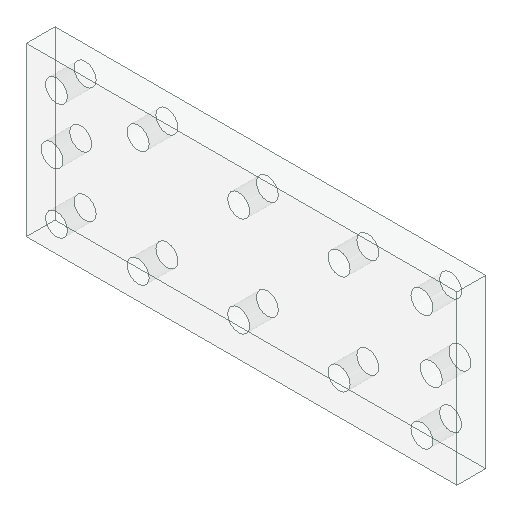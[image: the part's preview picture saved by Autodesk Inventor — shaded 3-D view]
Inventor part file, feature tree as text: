
AUTODESK INVENTOR PART (.ipt)
format: ipt  version: 2025 (Build 290162000, 162)  size: 122,880 bytes
history: native  units: mm
features: other x1, extrude x1, sketch x1
ambient origin geometry x8: Origin, YZ Plane, XZ Plane, XY Plane, X Axis, Y Axis, Z Axis, Center Point
bodies: Body1 (feature_tree)
feature tree (3):
  other  "Sólido1"
  extrude  "Extrusão1"  [1 undecoded]
  sketch  "Esboço1"  dims[d0=6.0mm d1=0.0mm]
note: 1 required parameter value undecoded (feature->parameter linkage not recoverable at this tier; creation-order binding heuristic only, values carry confidence <= 0.55)
